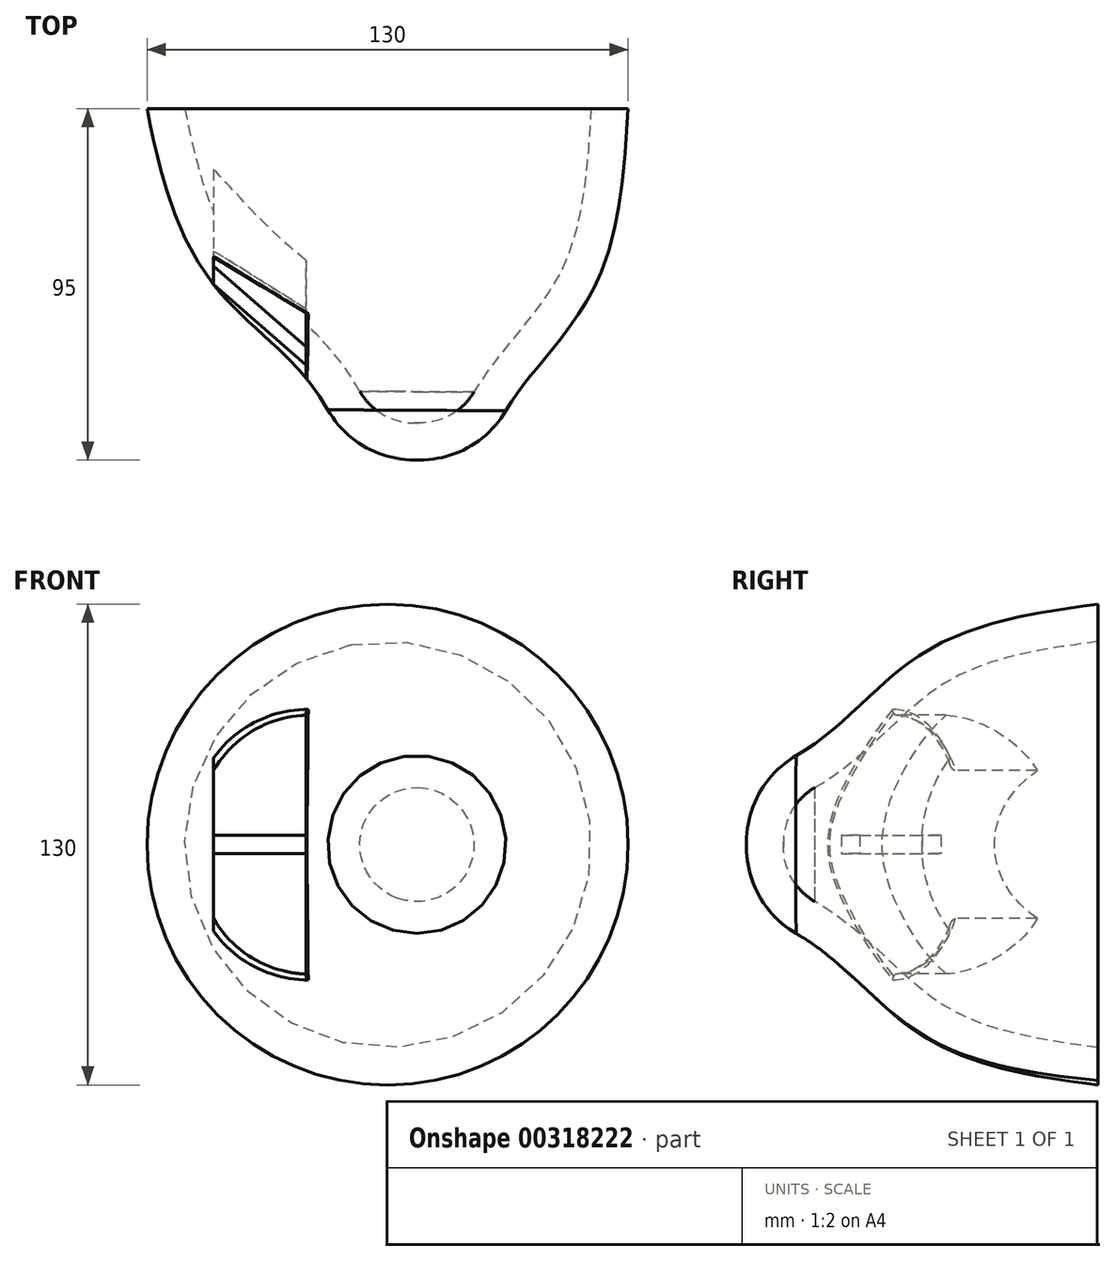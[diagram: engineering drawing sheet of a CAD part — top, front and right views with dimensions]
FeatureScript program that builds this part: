
annotation { "Feature Type Name" : "Feature", "Feature Type Description" : "" }
export const myFeature = defineFeature(function(context is Context, id is Id, definition is map)
    precondition{}
    {
        {
            var Q0;
            Q0=qCreatedBy(makeId("Front.planeOp"),FACE);
            var sketch = newSketch(context, id + "F0", { "sketchPlane" : qUnion([Q0])});
            skCircle(sketch, "E0", {"center": v(0, 0) * mm, "radius": 25 * mm});
            skSolve(sketch);
        }
        {
            var Q0;
            Q0=qCreatedBy(makeId("Front.planeOp"),FACE);
            cPlane(context, id + "F1", {"entities" : qUnion([Q0]), "cplaneType" : CPlaneType.OFFSET, "offset" : 30 * mm, "oppositeDirection" : true, "width" : 150 * mm, "height" : 150 * mm});
        }
        {
            var Q0;
            Q0=qCreatedBy(id+"F1.planeOp",FACE);
            var sketch = newSketch(context, id + "F2", { "sketchPlane" : qUnion([Q0])});
            skCircle(sketch, "E1", {"center": v(-3, 0) * mm, "radius": 50 * mm});
            skSolve(sketch);
        }
        {
            var Q0;
            Q0=qCreatedBy(id+"F1.planeOp",FACE);
            cPlane(context, id + "F3", {"entities" : qUnion([Q0]), "cplaneType" : CPlaneType.OFFSET, "offset" : 20 * mm, "width" : 150 * mm, "height" : 150 * mm});
        }
        {
            var Q0;
            Q0=qCreatedBy(id+"F3.planeOp",FACE);
            var sketch = newSketch(context, id + "F4", { "sketchPlane" : qUnion([Q0])});
            skCircle(sketch, "E2", {"center": v(0, 0) * mm, "radius": 32.5 * mm});
            skSolve(sketch);
        }
        {
            var Q0;
            Q0=qCreatedBy(id+"F1.planeOp",FACE);
            cPlane(context, id + "F5", {"entities" : qUnion([Q0]), "cplaneType" : CPlaneType.OFFSET, "offset" : 50 * mm, "oppositeDirection" : true, "width" : 150 * mm, "height" : 150 * mm});
        }
        {
            var Q0;
            Q0=qCreatedBy(id+"F5.planeOp",FACE);
            var sketch = newSketch(context, id + "F6", { "sketchPlane" : qUnion([Q0])});
            skCircle(sketch, "E3", {"center": v(-8, 0) * mm, "radius": 65 * mm});
            skSolve(sketch);
        }
        {
            var Q0;
            Q0=qCreatedBy(makeId("Front.planeOp"),FACE);
            cPlane(context, id + "F7", {"entities" : qUnion([Q0]), "cplaneType" : CPlaneType.OFFSET, "offset" : 15 * mm, "width" : 150 * mm, "height" : 150 * mm});
        }
        {
            var Q0;
            Q0=qCreatedBy(id+"F7.planeOp",FACE);
            var sketch = newSketch(context, id + "F8", { "sketchPlane" : qUnion([Q0])});
            skCircle(sketch, "E4", {"center": v(0, 0) * mm, "radius": 17.5 * mm});
            skSolve(sketch);
        }
        {
            var Q0;
            Q0 = qSketchRegion(id + "F8", true);
            var Q1;
            Q1 = qSketchRegion(id + "F0", true);
            var Q2;
            Q2 = qSketchRegion(id + "F4", true);
            var Q3;
            Q3 = qSketchRegion(id + "F2", true);
            var Q4;
            Q4 = qSketchRegion(id + "F6", true);
            loft(context, id + "F9", {"sheetProfilesArray" : [{ "sheetProfileEntities" : qUnion([Q0]) }, { "sheetProfileEntities" : qUnion([Q1]) }, { "sheetProfileEntities" : qUnion([Q2]) }, { "sheetProfileEntities" : qUnion([Q3]) }, { "sheetProfileEntities" : qUnion([Q4]) }]});
        }
        {
            var Q0;
            Q0=makeQuery(id+"F9.opLoft","MID_CAP_EDGE",EDGE,{"disambiguationData":[OSD([sQuery(id+"F8.wireOp",EDGE,"E4")])],"capPos":0.0});
            fillet(context, id + "F10", {"entities" : qUnion([Q0]), "radius" : 27 * mm, "tangentPropagation" : true, "allowEdgeOverflow" : false});
        }
        {
            var Q0;
            Q0=makeQuery(id+"F9.opLoft","CAP_FACE",FACE,{"disambiguationData":[OSD([makeQuery(id+"F6.imprint","IMPRINT",FACE,{"disambiguationData":[TD([[makeQuery(id+"F6.imprint","IMPRINT",EDGE,{"derivedFrom":sQuery(id+"F6.wireOp",EDGE,"E3")}),1.0]])]})])],"isStart":true});
            shell(context, id + "F11", {"entities" : qUnion([Q0]), "thickness" : 10 * mm});
        }
        {
            var Q0;
            Q0=qCreatedBy(makeId("Front.planeOp"),FACE);
            var sketch = newSketch(context, id + "F12", { "sketchPlane" : qUnion([Q0])});
            skLineSegment(sketch, "E5", {"start": v(-30, -35) * mm, "end": v(-30, 35) * mm});
            skLineSegment(sketch, "E6", {"start": v(-55, -20) * mm, "end": v(-55, 20) * mm});
            skArc(sketch, "E7", {"start": v(-55, -20) * mm, "mid": v(-44.44, -30.74) * mm, "end": v(-30, -35) * mm});
            skArc(sketch, "E8", {"start": v(-30, 35) * mm, "mid": v(-44.44, 30.74) * mm, "end": v(-55, 20) * mm});
            skSolve(sketch);
        }
        {
            var Q0;
            Q0 = qSketchRegion(id + "F12", true);
            extrude(context, id + "F13", {"entities" : qUnion([Q0]), "operationType" : NewBodyOperationType.REMOVE, "endBound" : BoundingType.THROUGH_ALL, "oppositeDirection" : true, "depth" : 25 * mm});
        }
        {
            var Q0;
            Q0=makeQuery(id+"F13.boolean.opBoolean","COPY",FACE,{"derivedFrom":makeQuery(id+"F13.opExtrude","SWEPT_FACE",FACE,{"disambiguationData":[OSD([sQuery(id+"F12.wireOp",EDGE,"E5")])]})});
            var sketch = newSketch(context, id + "F14", { "sketchPlane" : qUnion([Q0])});
            skLineSegment(sketch, "E9.bottom", {"start": v(-15.62, 2.5) * mm, "end": v(-10.62, 2.5) * mm});
            skLineSegment(sketch, "E9.top", {"start": v(-15.62, -2.5) * mm, "end": v(-10.62, -2.5) * mm});
            skLineSegment(sketch, "E9.left", {"start": v(-15.62, 2.5) * mm, "end": v(-15.62, -2.5) * mm});
            skLineSegment(sketch, "E9.right", {"start": v(-10.62, 2.5) * mm, "end": v(-10.62, -2.5) * mm});
            skPoint(sketch, "E9.middle", {"position": v(-13.12, 0) * mm});
            skSolve(sketch);
        }
        {
            var Q0;
            Q0=makeQuery(id+"F13.boolean.opBoolean","COPY",FACE,{"derivedFrom":makeQuery(id+"F13.opExtrude","SWEPT_FACE",FACE,{"disambiguationData":[OSD([sQuery(id+"F12.wireOp",EDGE,"E6")])]})});
            var sketch = newSketch(context, id + "F15", { "sketchPlane" : qUnion([Q0])});
            skLineSegment(sketch, "E10.bottom", {"start": v(37.5, 2.5) * mm, "end": v(32.5, 2.5) * mm});
            skLineSegment(sketch, "E10.top", {"start": v(37.5, -2.5) * mm, "end": v(32.5, -2.5) * mm});
            skLineSegment(sketch, "E10.left", {"start": v(37.5, 2.5) * mm, "end": v(37.5, -2.5) * mm});
            skLineSegment(sketch, "E10.right", {"start": v(32.5, 2.5) * mm, "end": v(32.5, -2.5) * mm});
            skPoint(sketch, "E10.middle", {"position": v(35, 0) * mm});
            skSolve(sketch);
        }
        {
            var Q1;
            Q1 = qSketchRegion(id + "F14", true);
            var Q2;
            Q2 = qSketchRegion(id + "F15", true);
            loft(context, id + "F16", {"operationType" : NewBodyOperationType.ADD, "sheetProfilesArray" : [{ "sheetProfileEntities" : qUnion([Q1]) }, { "sheetProfileEntities" : qUnion([Q2]) }]});
        }
        {
            var Q0;
            Q0=makeQuery(id+"F13.boolean.opBoolean","INTERSECT",EDGE,{"derivedFrom":[makeQuery(id+"F9.opLoft","SWEPT_FACE",FACE,{"disambiguationData":[OSD([sQuery(id+"F0.wireOp",EDGE,"E0"),sQuery(id+"F8.wireOp",EDGE,"E4")])]}),makeQuery(id+"F13.opExtrude","SWEPT_FACE",FACE,{"disambiguationData":[OSD([sQuery(id+"F12.wireOp",EDGE,"E5")])]})]});
            var Q1;
            Q1=makeQuery(id+"F13.boolean.opBoolean","INTERSECT",EDGE,{"derivedFrom":[makeQuery(id+"F9.opLoft","SWEPT_FACE",FACE,{"disambiguationData":[OSD([sQuery(id+"F0.wireOp",EDGE,"E0"),sQuery(id+"F8.wireOp",EDGE,"E4")])]}),makeQuery(id+"F13.opExtrude","SWEPT_FACE",FACE,{"disambiguationData":[OSD([sQuery(id+"F12.wireOp",EDGE,"E7")])]})]});
            var Q2;
            Q2=makeQuery(id+"F13.boolean.opBoolean","INTERSECT",EDGE,{"derivedFrom":[makeQuery(id+"F9.opLoft","SWEPT_FACE",FACE,{"disambiguationData":[OSD([sQuery(id+"F0.wireOp",EDGE,"E0"),sQuery(id+"F8.wireOp",EDGE,"E4")])]}),makeQuery(id+"F13.opExtrude","SWEPT_FACE",FACE,{"disambiguationData":[OSD([sQuery(id+"F12.wireOp",EDGE,"E8")])]})]});
            fillet(context, id + "F17", {"entities" : qUnion([Q0, Q1, Q2]), "radius" : 1 * mm, "tangentPropagation" : true, "allowEdgeOverflow" : false});
        }
    });
